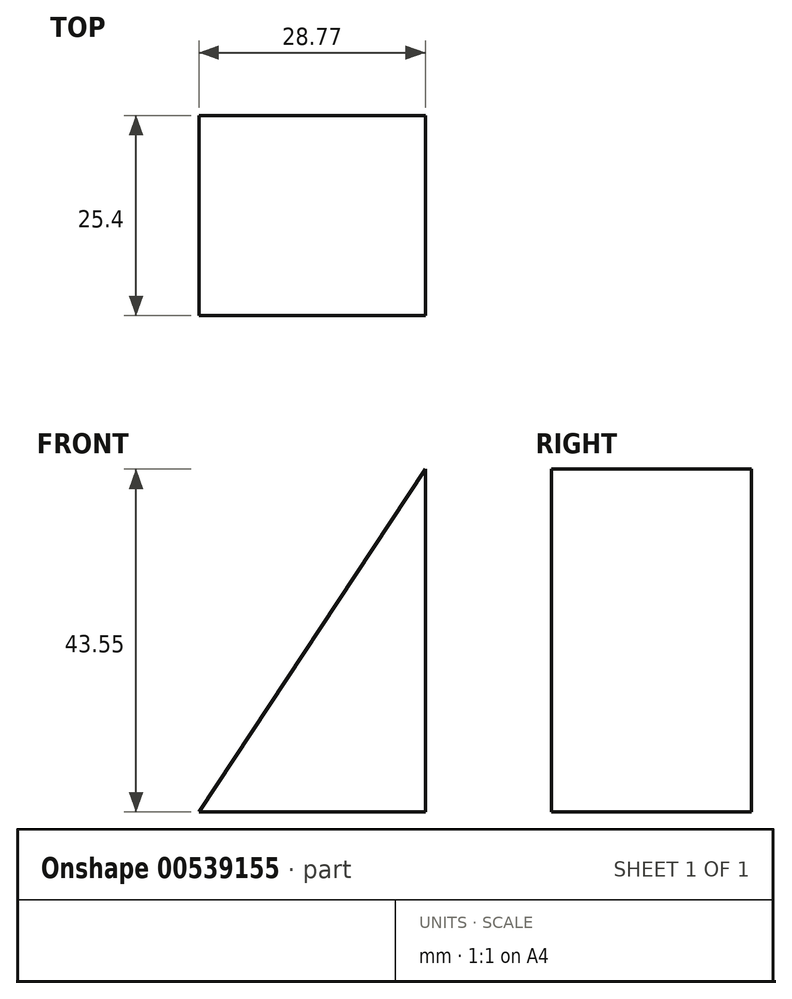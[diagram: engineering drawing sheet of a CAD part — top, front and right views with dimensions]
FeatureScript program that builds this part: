
annotation { "Feature Type Name" : "Feature", "Feature Type Description" : "" }
export const myFeature = defineFeature(function(context is Context, id is Id, definition is map)
    precondition{}
    {
        {
            var Q0;
            Q0=qCreatedBy(makeId("Front.planeOp"),FACE);
            var sketch = newSketch(context, id + "F0", { "sketchPlane" : qUnion([Q0])});
            skLineSegment(sketch, "E0", {"start": v(0, 0) * mm, "end": v(28.77, 43.55) * mm});
            skLineSegment(sketch, "E1", {"start": v(28.77, 43.55) * mm, "end": v(28.77, 0) * mm});
            skLineSegment(sketch, "E2", {"start": v(28.77, 0) * mm, "end": v(0, 0) * mm});
            skSolve(sketch);
        }
        {
            var Q0;
            Q0 = qSketchRegion(id + "F0", true);
            extrude(context, id + "F1", {"entities" : qUnion([Q0]), "depth" : 25.4 * mm, "offsetDistance" : 25.4 * mm});
        }
    });
